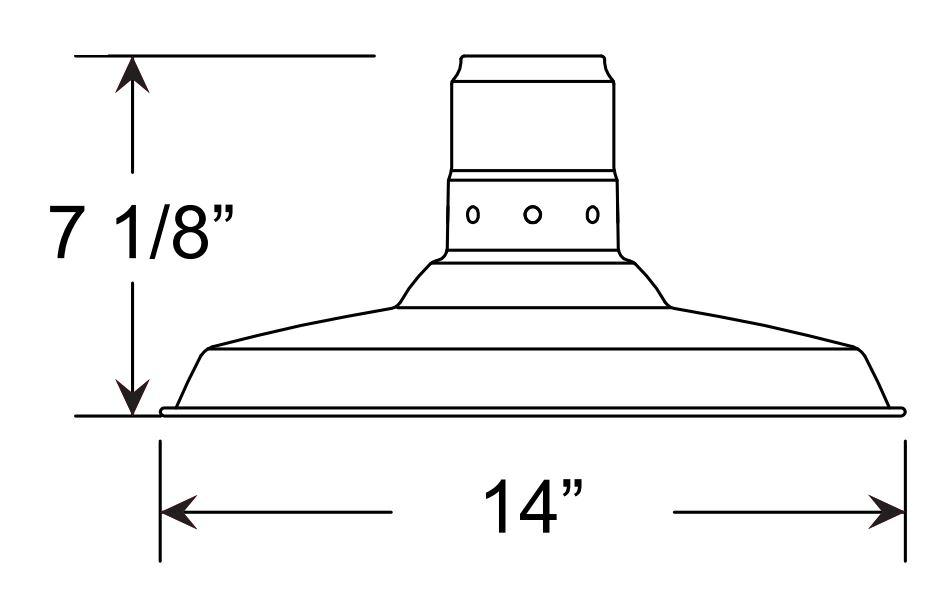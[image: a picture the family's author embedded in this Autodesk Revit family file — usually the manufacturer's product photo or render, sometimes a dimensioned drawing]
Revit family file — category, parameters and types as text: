
# Revit family: Mini Bella Vista_Bell_MB
name_source: partatom
category: Lighting Fixtures
units: mm (PartAtom-declared; Revit-internal decimal feet)

## family parameters
Always vertical = Yes
Cut with Voids When Loaded = No
Light Source = Yes
OmniClass Number = 23.80.70.00
OmniClass Title = Lighting
Part Type = Normal
Room Calculation Point = No
Round Connector Dimension = Use Diameter
Shared = No
Work Plane-Based = No

## types (3) — shared parameters
Body Colour = Spun aluminium
Body Material = body
Bulb = BULB
CRI = >90
Color Filter = 16777215
Construction Material = Heavy Duty spun aluminum.
Default Elevation = 0' - 0"
Description = 120-277 Voltage
Dimming = 1%
Dimming Lamp Color Temperature Shift = <None>
Efficiency = 65-125 lumens per watt
GLASS = Glass
Inside body material = INSIDE BODY MATERIAL
Life = L70 50,000 hours
Load Classification = Lighting
Manufacturer = ANP Lighting
Power Factor = 1
Tilt Angle = 90.00°
URL = https://www.anplighting.com
Voltage = 277 V
Warranty = 5 year limited warranty

## per-type parameters (varying)
| type | Apparent Load | Fixture Diameter | Fixture Height | Lamp | MBVB12 | MBVB14 | MBVB16 | Photometric Web File | Wattage Comments | Weight |
| MBVB12 | 100 VA | 1' - 0" | 0' - 10 1/2" | 100W MAX MEDIUM BASE | Yes | No | No | MBVB12M016LDDW40K-IES.ies | 100W Max | 0.8 lb |
| MBVB14 | 200 VA | 1' - 2" | 0' - 11 1/2" | 200W MAX MEDIUM BASE | No | Yes | No | MBVB16E030LDST540K.ies | 200W Max | 0.95 lb |
| MBVB16 | 200 VA | 1' - 4" | 1' - 0 1/2" | 200W MAX MEDIUM BASE | No | No | Yes | MBVA16E040LDST540K.ies | 200W | 1.25 lb |

note: column(s) folded — value = type name in every type: Model

## geometry (parser evidence)
native form markers: Sweep x30
no freeform markers — native parametric forms only
